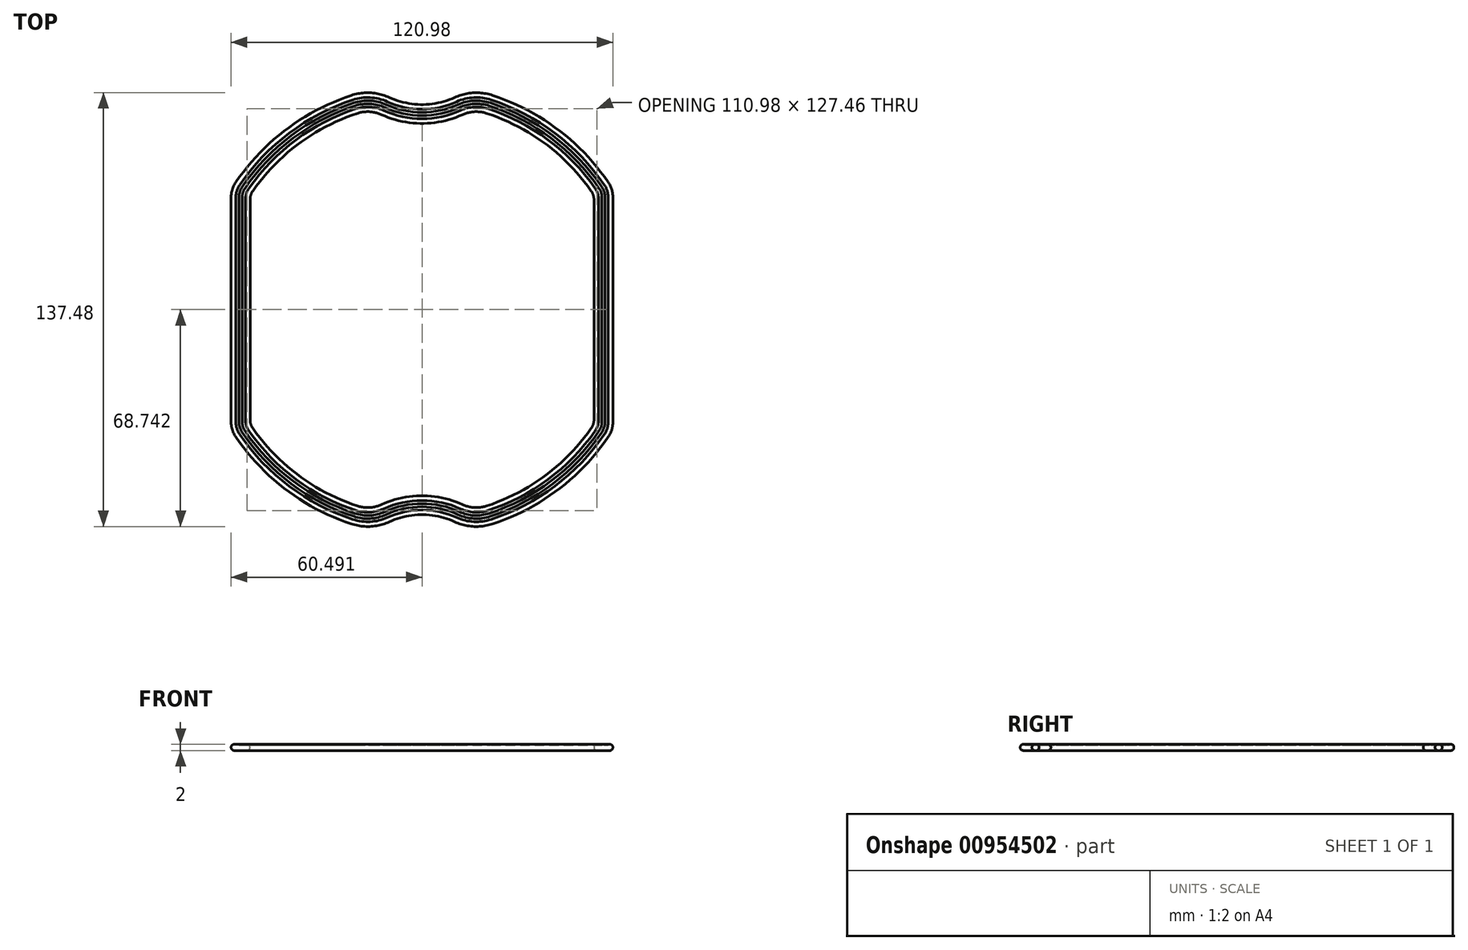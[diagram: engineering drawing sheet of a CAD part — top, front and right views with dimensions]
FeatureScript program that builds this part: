
annotation { "Feature Type Name" : "Feature", "Feature Type Description" : "" }
export const myFeature = defineFeature(function(context is Context, id is Id, definition is map)
    precondition{}
    {
        {
            var Q0;
            Q0=qCreatedBy(makeId("Top.planeOp"),FACE);
            var sketch = newSketch(context, id + "F0", { "sketchPlane" : qUnion([Q0])});
            skArc(sketch, "E0.0", {"start": v(-51.54, 42.6) * mm, "mid": v(-35.5, 59.37) * mm, "end": v(-14.91, 70.12) * mm});
            skArc(sketch, "E0.2", {"start": v(-13.04, 64.42) * mm, "mid": v(-9.18, 64.93) * mm, "end": v(-5.4, 64) * mm});
            skArc(sketch, "E0.3", {"start": v(-14.91, 70.12) * mm, "mid": v(-8.85, 70.92) * mm, "end": v(-2.9, 69.46) * mm});
            skArc(sketch, "E0.4", {"start": v(-2.9, 69.46) * mm, "mid": v(7.46, 67.21) * mm, "end": v(17.83, 69.46) * mm});
            skArc(sketch, "E0.5", {"start": v(20.32, 64) * mm, "mid": v(7.46, 61.21) * mm, "end": v(-5.4, 64) * mm});
            skArc(sketch, "E1.0", {"start": v(-53.03, 37.8) * mm, "mid": v(-52.65, 40.3) * mm, "end": v(-51.54, 42.6) * mm});
            skArc(sketch, "E2.0", {"start": v(-46.12, 39.89) * mm, "mid": v(-31.56, 54.82) * mm, "end": v(-13.04, 64.42) * mm});
            skArc(sketch, "E2.1", {"start": v(-46.12, 39.89) * mm, "mid": v(-46.8, 38.52) * mm, "end": v(-47.03, 37.01) * mm});
            skLineSegment(sketch, "E2.2", {"start": v(-47.03, -32.59) * mm, "end": v(-47.03, 37.01) * mm});
            skLineSegment(sketch, "E3.0", {"start": v(-53.03, -33.37) * mm, "end": v(-53.03, 37.8) * mm});
            skArc(sketch, "E4.0", {"start": v(-51.54, -38.17) * mm, "mid": v(-52.65, -35.88) * mm, "end": v(-53.03, -33.37) * mm});
            skArc(sketch, "E4.1", {"start": v(-47.03, -32.59) * mm, "mid": v(-46.8, -34.1) * mm, "end": v(-46.12, -35.46) * mm});
            skArc(sketch, "E4.2", {"start": v(-13.04, -60) * mm, "mid": v(-31.56, -50.4) * mm, "end": v(-46.12, -35.46) * mm});
            skArc(sketch, "E4.3", {"start": v(-14.91, -65.7) * mm, "mid": v(-35.5, -54.95) * mm, "end": v(-51.54, -38.17) * mm});
            skArc(sketch, "E5.0", {"start": v(-5.4, -59.58) * mm, "mid": v(-9.18, -60.51) * mm, "end": v(-13.04, -60) * mm});
            skArc(sketch, "E5.1", {"start": v(-2.9, -65.04) * mm, "mid": v(-8.85, -66.5) * mm, "end": v(-14.91, -65.7) * mm});
            skArc(sketch, "E6.0", {"start": v(-5.4, -59.58) * mm, "mid": v(7.46, -56.79) * mm, "end": v(20.32, -59.58) * mm});
            skArc(sketch, "E6.1", {"start": v(17.83, -65.04) * mm, "mid": v(7.46, -62.79) * mm, "end": v(-2.9, -65.04) * mm});
            skArc(sketch, "E6.2", {"start": v(27.96, -60) * mm, "mid": v(24.1, -60.51) * mm, "end": v(20.32, -59.58) * mm});
            skArc(sketch, "E6.3", {"start": v(29.84, -65.7) * mm, "mid": v(23.77, -66.5) * mm, "end": v(17.83, -65.04) * mm});
            skArc(sketch, "E6.4", {"start": v(61.04, -35.46) * mm, "mid": v(46.48, -50.4) * mm, "end": v(27.96, -60) * mm});
            skArc(sketch, "E6.5", {"start": v(66.47, -38.17) * mm, "mid": v(50.42, -54.95) * mm, "end": v(29.84, -65.7) * mm});
            skArc(sketch, "E7.0", {"start": v(61.04, -35.46) * mm, "mid": v(61.72, -34.1) * mm, "end": v(61.95, -32.59) * mm});
            skArc(sketch, "E7.1", {"start": v(67.95, -33.37) * mm, "mid": v(67.57, -35.88) * mm, "end": v(66.47, -38.17) * mm});
            skLineSegment(sketch, "E7.2", {"start": v(67.95, 37.8) * mm, "end": v(67.95, -33.37) * mm});
            skLineSegment(sketch, "E7.3", {"start": v(61.95, -32.59) * mm, "end": v(61.95, 37.01) * mm});
            skArc(sketch, "E8.0", {"start": v(66.47, 42.6) * mm, "mid": v(67.57, 40.3) * mm, "end": v(67.95, 37.8) * mm});
            skArc(sketch, "E8.1", {"start": v(61.95, 37.01) * mm, "mid": v(61.72, 38.52) * mm, "end": v(61.04, 39.89) * mm});
            skArc(sketch, "E8.2", {"start": v(27.96, 64.42) * mm, "mid": v(46.48, 54.82) * mm, "end": v(61.04, 39.89) * mm});
            skArc(sketch, "E8.3", {"start": v(29.84, 70.12) * mm, "mid": v(50.42, 59.37) * mm, "end": v(66.47, 42.6) * mm});
            skArc(sketch, "E9.0", {"start": v(20.32, 64) * mm, "mid": v(24.1, 64.93) * mm, "end": v(27.96, 64.42) * mm});
            skArc(sketch, "E9.1", {"start": v(17.83, 69.46) * mm, "mid": v(23.77, 70.92) * mm, "end": v(29.84, 70.12) * mm});
            skSolve(sketch);
        }
        {
            var Q0;
            Q0 = qSketchRegion(id + "F0", true);
            extrude(context, id + "F1", {"entities" : qUnion([Q0]), "depth" : 2 * mm, "offsetDistance" : 25 * mm});
        }
        {
            var Q0;
            Q0=makeQuery(id+"F1.opExtrude","CAP_EDGE",EDGE,{"disambiguationData":[OSD([sQuery(id+"F0.wireOp",EDGE,"E3.0")])],"isStart":true});
            var Q1;
            Q1=makeQuery(id+"F1.opExtrude","CAP_EDGE",EDGE,{"disambiguationData":[OSD([sQuery(id+"F0.wireOp",EDGE,"E3.0")])],"isStart":false});
            var Q2;
            Q2=makeQuery(id+"F1.opExtrude","CAP_EDGE",EDGE,{"disambiguationData":[OSD([sQuery(id+"F0.wireOp",EDGE,"E2.2")])],"isStart":false});
            var Q3;
            Q3=makeQuery(id+"F1.opExtrude","CAP_EDGE",EDGE,{"disambiguationData":[OSD([sQuery(id+"F0.wireOp",EDGE,"E2.2")])],"isStart":true});
            fillet(context, id + "F2", {"entities" : qUnion([Q0, Q1, Q2, Q3]), "tangentPropagation" : true, "radius" : 1 * mm, "defaultsChanged" : false, "vertexSettings" : [], "allowEdgeOverflow" : false});
        }
        {
            var Q0;
            Q0=makeQuery(id+"F1.opExtrude","CAP_FACE",FACE,{"disambiguationData":[OSD([sQuery(id+"F0.wireOp",EDGE,"E0.0"),sQuery(id+"F0.wireOp",EDGE,"E0.2"),sQuery(id+"F0.wireOp",EDGE,"E0.3"),sQuery(id+"F0.wireOp",EDGE,"E0.4"),sQuery(id+"F0.wireOp",EDGE,"E0.5"),sQuery(id+"F0.wireOp",EDGE,"E1.0"),sQuery(id+"F0.wireOp",EDGE,"E2.0"),sQuery(id+"F0.wireOp",EDGE,"E2.1"),sQuery(id+"F0.wireOp",EDGE,"E2.2"),sQuery(id+"F0.wireOp",EDGE,"E3.0"),sQuery(id+"F0.wireOp",EDGE,"E4.0"),sQuery(id+"F0.wireOp",EDGE,"E4.1"),sQuery(id+"F0.wireOp",EDGE,"E4.2"),sQuery(id+"F0.wireOp",EDGE,"E4.3"),sQuery(id+"F0.wireOp",EDGE,"E5.0"),sQuery(id+"F0.wireOp",EDGE,"E5.1"),sQuery(id+"F0.wireOp",EDGE,"E6.0"),sQuery(id+"F0.wireOp",EDGE,"E6.1"),sQuery(id+"F0.wireOp",EDGE,"E6.2"),sQuery(id+"F0.wireOp",EDGE,"E6.3"),sQuery(id+"F0.wireOp",EDGE,"E6.4"),sQuery(id+"F0.wireOp",EDGE,"E6.5"),sQuery(id+"F0.wireOp",EDGE,"E7.0"),sQuery(id+"F0.wireOp",EDGE,"E7.1"),sQuery(id+"F0.wireOp",EDGE,"E7.2"),sQuery(id+"F0.wireOp",EDGE,"E7.3"),sQuery(id+"F0.wireOp",EDGE,"E8.0"),sQuery(id+"F0.wireOp",EDGE,"E8.1"),sQuery(id+"F0.wireOp",EDGE,"E8.2"),sQuery(id+"F0.wireOp",EDGE,"E8.3"),sQuery(id+"F0.wireOp",EDGE,"E9.0"),sQuery(id+"F0.wireOp",EDGE,"E9.1")])],"isStart":false});
            var sketch = newSketch(context, id + "F3", { "sketchPlane" : qUnion([Q0])});
            skArc(sketch, "E10.0", {"start": v(29.05, -63.32) * mm, "mid": v(48.91, -52.95) * mm, "end": v(64.4, -36.76) * mm});
            skArc(sketch, "E10.1", {"start": v(18.87, -62.76) * mm, "mid": v(23.9, -64) * mm, "end": v(29.05, -63.32) * mm});
            skArc(sketch, "E10.2", {"start": v(-3.94, -62.76) * mm, "mid": v(7.46, -60.29) * mm, "end": v(18.87, -62.76) * mm});
            skArc(sketch, "E10.3", {"start": v(-14.13, -63.32) * mm, "mid": v(-8.99, -64) * mm, "end": v(-3.94, -62.76) * mm});
            skArc(sketch, "E10.4", {"start": v(-49.48, -36.76) * mm, "mid": v(-34, -52.95) * mm, "end": v(-14.13, -63.32) * mm});
            skArc(sketch, "E10.5", {"start": v(29.05, 67.75) * mm, "mid": v(23.9, 68.43) * mm, "end": v(18.87, 67.19) * mm});
            skArc(sketch, "E10.6", {"start": v(64.4, 41.18) * mm, "mid": v(48.91, 57.37) * mm, "end": v(29.05, 67.75) * mm});
            skArc(sketch, "E10.7", {"start": v(65.45, 37.8) * mm, "mid": v(65.18, 39.57) * mm, "end": v(64.4, 41.18) * mm});
            skLineSegment(sketch, "E10.8", {"start": v(65.45, -33.37) * mm, "end": v(65.45, 37.8) * mm});
            skArc(sketch, "E10.9", {"start": v(18.87, 67.19) * mm, "mid": v(7.46, 64.71) * mm, "end": v(-3.94, 67.19) * mm});
            skArc(sketch, "E10.10", {"start": v(-3.94, 67.19) * mm, "mid": v(-8.99, 68.43) * mm, "end": v(-14.13, 67.75) * mm});
            skArc(sketch, "E10.11", {"start": v(-14.13, 67.75) * mm, "mid": v(-34, 57.37) * mm, "end": v(-49.48, 41.18) * mm});
            skArc(sketch, "E10.12", {"start": v(-49.48, 41.18) * mm, "mid": v(-50.26, 39.57) * mm, "end": v(-50.53, 37.8) * mm});
            skLineSegment(sketch, "E10.13", {"start": v(-50.53, 37.8) * mm, "end": v(-50.53, -33.37) * mm});
            skArc(sketch, "E10.14", {"start": v(64.4, -36.76) * mm, "mid": v(65.18, -35.14) * mm, "end": v(65.45, -33.37) * mm});
            skArc(sketch, "E10.15", {"start": v(-50.53, -33.37) * mm, "mid": v(-50.26, -35.14) * mm, "end": v(-49.48, -36.76) * mm});
            skArc(sketch, "E11.0", {"start": v(19.28, -61.85) * mm, "mid": v(23.96, -63) * mm, "end": v(28.74, -62.37) * mm});
            skArc(sketch, "E11.1", {"start": v(-4.36, -61.85) * mm, "mid": v(7.46, -59.29) * mm, "end": v(19.28, -61.85) * mm});
            skArc(sketch, "E11.2", {"start": v(-13.82, -62.37) * mm, "mid": v(-9.04, -63) * mm, "end": v(-4.36, -61.85) * mm});
            skArc(sketch, "E11.3", {"start": v(-48.65, -36.2) * mm, "mid": v(-33.4, -52.15) * mm, "end": v(-13.82, -62.37) * mm});
            skArc(sketch, "E11.4", {"start": v(-49.53, -33.37) * mm, "mid": v(-49.3, -34.85) * mm, "end": v(-48.65, -36.2) * mm});
            skArc(sketch, "E11.5", {"start": v(63.58, 40.62) * mm, "mid": v(48.31, 56.57) * mm, "end": v(28.74, 66.8) * mm});
            skArc(sketch, "E11.6", {"start": v(64.45, 37.8) * mm, "mid": v(64.23, 39.27) * mm, "end": v(63.58, 40.62) * mm});
            skLineSegment(sketch, "E11.7", {"start": v(64.45, -33.37) * mm, "end": v(64.45, 37.8) * mm});
            skArc(sketch, "E11.8", {"start": v(63.58, -36.2) * mm, "mid": v(64.23, -34.85) * mm, "end": v(64.45, -33.37) * mm});
            skArc(sketch, "E11.9", {"start": v(28.74, 66.8) * mm, "mid": v(23.96, 67.43) * mm, "end": v(19.28, 66.28) * mm});
            skArc(sketch, "E11.10", {"start": v(19.28, 66.28) * mm, "mid": v(7.46, 63.71) * mm, "end": v(-4.36, 66.28) * mm});
            skArc(sketch, "E11.11", {"start": v(-4.36, 66.28) * mm, "mid": v(-9.04, 67.43) * mm, "end": v(-13.82, 66.8) * mm});
            skArc(sketch, "E11.12", {"start": v(-13.82, 66.8) * mm, "mid": v(-33.4, 56.57) * mm, "end": v(-48.65, 40.62) * mm});
            skArc(sketch, "E11.13", {"start": v(-48.65, 40.62) * mm, "mid": v(-49.3, 39.27) * mm, "end": v(-49.53, 37.8) * mm});
            skArc(sketch, "E11.14", {"start": v(28.74, -62.37) * mm, "mid": v(48.31, -52.15) * mm, "end": v(63.58, -36.2) * mm});
            skLineSegment(sketch, "E11.15", {"start": v(-49.53, 37.8) * mm, "end": v(-49.53, -33.37) * mm});
            skArc(sketch, "E12.0", {"start": v(-14.44, -64.27) * mm, "mid": v(-8.93, -65) * mm, "end": v(-3.53, -63.67) * mm});
            skArc(sketch, "E12.1", {"start": v(-50.3, -37.32) * mm, "mid": v(-34.6, -53.75) * mm, "end": v(-14.44, -64.27) * mm});
            skArc(sketch, "E12.2", {"start": v(-51.53, -33.37) * mm, "mid": v(-51.22, -35.44) * mm, "end": v(-50.3, -37.32) * mm});
            skLineSegment(sketch, "E12.3", {"start": v(-51.53, 37.8) * mm, "end": v(-51.53, -33.37) * mm});
            skArc(sketch, "E12.4", {"start": v(-50.3, 41.75) * mm, "mid": v(-51.22, 39.86) * mm, "end": v(-51.53, 37.8) * mm});
            skLineSegment(sketch, "E12.5", {"start": v(66.45, -33.37) * mm, "end": v(66.45, 37.8) * mm});
            skArc(sketch, "E12.6", {"start": v(65.23, -37.32) * mm, "mid": v(66.14, -35.44) * mm, "end": v(66.45, -33.37) * mm});
            skArc(sketch, "E12.7", {"start": v(29.37, -64.27) * mm, "mid": v(49.51, -53.75) * mm, "end": v(65.23, -37.32) * mm});
            skArc(sketch, "E12.8", {"start": v(18.45, -63.67) * mm, "mid": v(23.85, -65) * mm, "end": v(29.37, -64.27) * mm});
            skArc(sketch, "E12.9", {"start": v(66.45, 37.8) * mm, "mid": v(66.14, 39.86) * mm, "end": v(65.23, 41.75) * mm});
            skArc(sketch, "E12.10", {"start": v(65.23, 41.75) * mm, "mid": v(49.51, 58.17) * mm, "end": v(29.37, 68.7) * mm});
            skArc(sketch, "E12.11", {"start": v(29.37, 68.7) * mm, "mid": v(23.85, 69.43) * mm, "end": v(18.45, 68.1) * mm});
            skArc(sketch, "E12.12", {"start": v(18.45, 68.1) * mm, "mid": v(7.46, 65.71) * mm, "end": v(-3.53, 68.1) * mm});
            skArc(sketch, "E12.13", {"start": v(-3.53, 68.1) * mm, "mid": v(-8.93, 69.43) * mm, "end": v(-14.44, 68.7) * mm});
            skArc(sketch, "E12.14", {"start": v(-3.53, -63.67) * mm, "mid": v(7.46, -61.29) * mm, "end": v(18.45, -63.67) * mm});
            skArc(sketch, "E12.15", {"start": v(-14.44, 68.7) * mm, "mid": v(-34.6, 58.17) * mm, "end": v(-50.3, 41.75) * mm});
            skArc(sketch, "E13.0", {"start": v(63.45, -32.59) * mm, "mid": v(63.15, -34.55) * mm, "end": v(62.27, -36.33) * mm});
            skLineSegment(sketch, "E13.1", {"start": v(63.45, 37.01) * mm, "end": v(63.45, -32.59) * mm});
            skArc(sketch, "E13.2", {"start": v(62.27, 40.75) * mm, "mid": v(63.15, 38.97) * mm, "end": v(63.45, 37.01) * mm});
            skArc(sketch, "E13.3", {"start": v(28.43, 65.85) * mm, "mid": v(47.37, 56.03) * mm, "end": v(62.27, 40.75) * mm});
            skArc(sketch, "E13.4", {"start": v(19.7, 65.37) * mm, "mid": v(24.02, 66.43) * mm, "end": v(28.43, 65.85) * mm});
            skArc(sketch, "E13.5", {"start": v(-13.5, -61.42) * mm, "mid": v(-32.45, -51.6) * mm, "end": v(-47.35, -36.33) * mm});
            skArc(sketch, "E13.6", {"start": v(-4.77, -60.95) * mm, "mid": v(-9.1, -62) * mm, "end": v(-13.5, -61.42) * mm});
            skArc(sketch, "E13.7", {"start": v(19.7, -60.95) * mm, "mid": v(7.46, -58.29) * mm, "end": v(-4.77, -60.95) * mm});
            skArc(sketch, "E13.8", {"start": v(28.43, -61.42) * mm, "mid": v(24.02, -62) * mm, "end": v(19.7, -60.95) * mm});
            skArc(sketch, "E13.9", {"start": v(-47.35, -36.33) * mm, "mid": v(-48.23, -34.55) * mm, "end": v(-48.53, -32.59) * mm});
            skLineSegment(sketch, "E13.10", {"start": v(-48.53, -32.59) * mm, "end": v(-48.53, 37.01) * mm});
            skArc(sketch, "E13.11", {"start": v(-48.53, 37.01) * mm, "mid": v(-48.23, 38.97) * mm, "end": v(-47.35, 40.75) * mm});
            skArc(sketch, "E13.12", {"start": v(-47.35, 40.75) * mm, "mid": v(-32.45, 56.03) * mm, "end": v(-13.5, 65.85) * mm});
            skArc(sketch, "E13.13", {"start": v(-13.5, 65.85) * mm, "mid": v(-9.1, 66.43) * mm, "end": v(-4.77, 65.37) * mm});
            skArc(sketch, "E13.14", {"start": v(62.27, -36.33) * mm, "mid": v(47.37, -51.6) * mm, "end": v(28.43, -61.42) * mm});
            skArc(sketch, "E13.15", {"start": v(-4.77, 65.37) * mm, "mid": v(7.46, 62.71) * mm, "end": v(19.7, 65.37) * mm});
            skSolve(sketch);
        }
        {
            var Q0;
            Q0=makeQuery(id+"F3.imprint","IMPRINT",FACE,{"disambiguationData":[TD([[makeQuery(id+"F3.imprint","IMPRINT",EDGE,{"derivedFrom":sQuery(id+"F3.wireOp",EDGE,"E10.0")}),-1.0]])]});
            var Q1;
            Q1=makeQuery(id+"F3.imprint","IMPRINT",FACE,{"disambiguationData":[TD([[makeQuery(id+"F3.imprint","IMPRINT",EDGE,{"derivedFrom":sQuery(id+"F3.wireOp",EDGE,"E11.0")}),1.0]])]});
            extrude(context, id + "F4", {"entities" : qUnion([Q0, Q1]), "operationType" : NewBodyOperationType.REMOVE, "oppositeDirection" : true, "depth" : 0.2 * mm, "offsetDistance" : 25 * mm});
        }
    });
